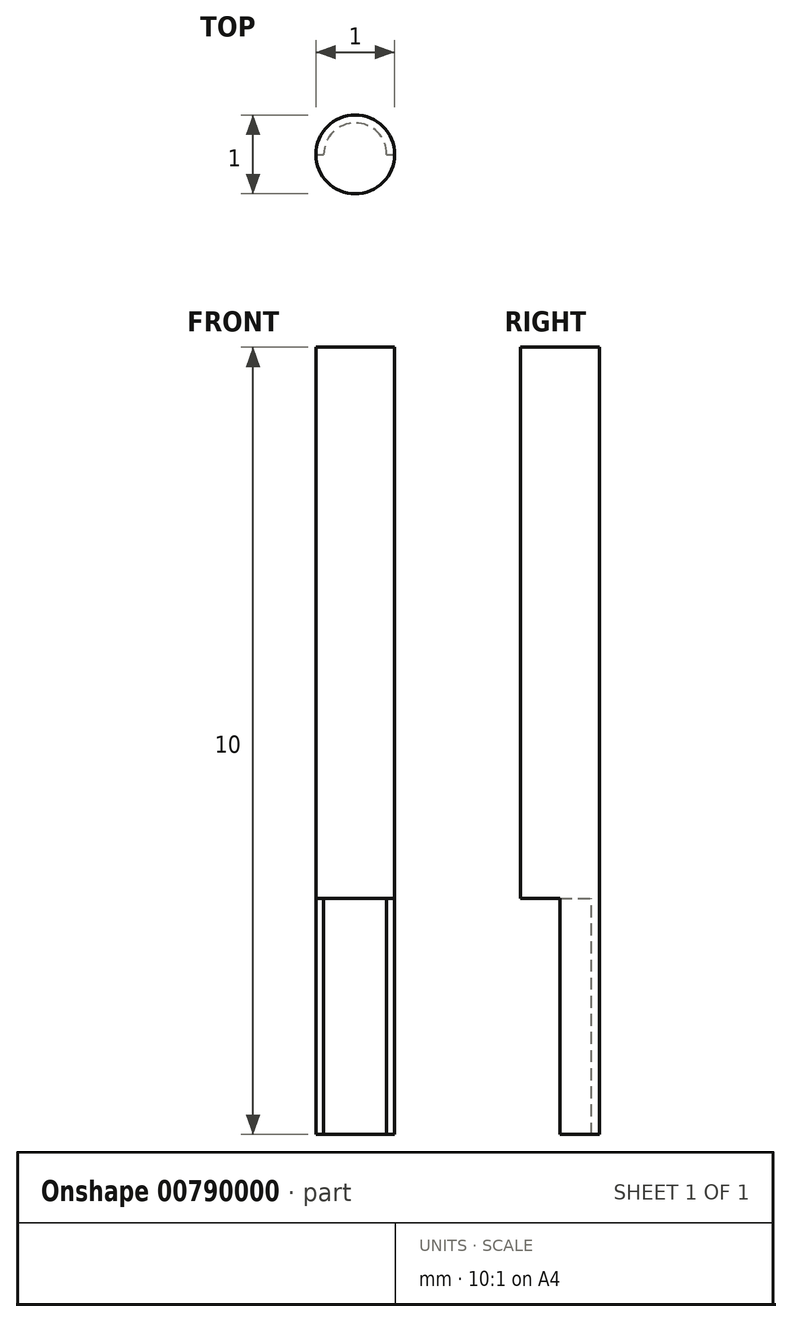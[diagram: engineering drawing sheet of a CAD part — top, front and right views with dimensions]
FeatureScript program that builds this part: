
annotation { "Feature Type Name" : "Feature", "Feature Type Description" : "" }
export const myFeature = defineFeature(function(context is Context, id is Id, definition is map)
    precondition{}
    {
        {
            var Q0;
            Q0=qCreatedBy(makeId("Top.planeOp"),FACE);
            var sketch = newSketch(context, id + "F0", { "sketchPlane" : qUnion([Q0])});
            skCircle(sketch, "E0", {"center": v(0, 0) * mm, "radius": 0.5 * mm});
            skSolve(sketch);
        }
        {
            var Q0;
            Q0 = qSketchRegion(id + "F0", true);
            extrude(context, id + "F1", {"entities" : qUnion([Q0]), "depth" : 7 * mm, "offsetDistance" : 25 * mm});
        }
        {
            var Q0;
            Q0=makeQuery(id+"F1.opExtrude","CAP_FACE",FACE,{"disambiguationData":[OSD([sQuery(id+"F0.wireOp",EDGE,"E0")])],"isStart":true});
            var sketch = newSketch(context, id + "F2", { "sketchPlane" : qUnion([Q0])});
            skArc(sketch, "E1", {"start": v(-0.5, 0) * mm, "mid": v(0, -0.5) * mm, "end": v(0.5, 0) * mm});
            skArc(sketch, "E2", {"start": v(-0.4, 0) * mm, "mid": v(0, -0.4) * mm, "end": v(0.4, 0) * mm});
            skLineSegment(sketch, "E3", {"start": v(-0.5, 0) * mm, "end": v(-0.4, 0) * mm});
            skLineSegment(sketch, "E4", {"start": v(0.4, 0) * mm, "end": v(0.5, 0) * mm});
            skSolve(sketch);
        }
        {
            var Q0;
            Q0 = qSketchRegion(id + "F2", true);
            extrude(context, id + "F3", {"entities" : qUnion([Q0]), "operationType" : NewBodyOperationType.ADD, "depth" : 3 * mm, "offsetDistance" : 25 * mm});
        }
    });
